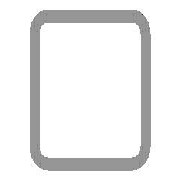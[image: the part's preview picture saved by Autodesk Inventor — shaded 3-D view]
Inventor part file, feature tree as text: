
AUTODESK INVENTOR PART (.ipt)
format: ipt  version: 2025.1 (Build 291241020, 241B)  size: 135,168 bytes
history: native  units: mm (DEFAULTED — no unit token found)
features: other x4, sketch x1, plane x1
ambient origin geometry x8: Origin, YZ Plane, XZ Plane, XY Plane, X Axis, Y Axis, Z Axis, Center Point
bodies: Solid1 (feature_tree), Body (feature_tree)
feature tree (6):
  parser-record x1  (decoder bookkeeping rows leaked as tree rows — omitted from the tree; the rows remain in map.json)
  other  "Driven Length"
  other  "Start Plane"
  other  "End Plane"
  sketch  "Sketch3"  dims[d3=4382.0mm d4=0.0mm d7=4.0mm d9=20.0mm d11=20.0mm d12=2.0mm d13=-0.0mm d14=4382.0mm d15=10.0mm d16=10.0mm d17=90.0deg d18=4382.0mm]
  plane  "Work Plane3"
